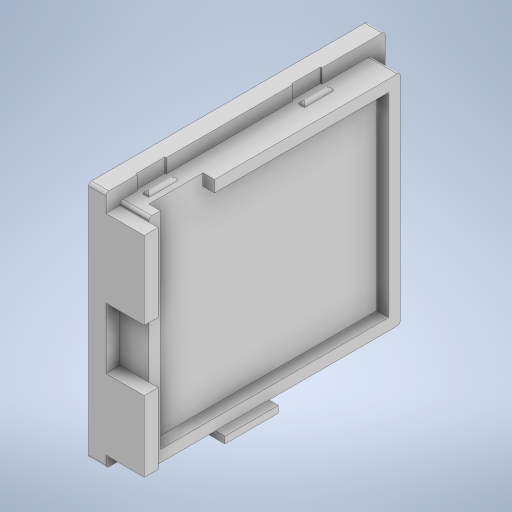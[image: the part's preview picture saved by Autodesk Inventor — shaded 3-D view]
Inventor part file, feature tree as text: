
AUTODESK INVENTOR PART (.ipt)
format: ipt  version: 2023 (Build 270158030, 158C)  size: 447,488 bytes
history: native  units: mm
features: extrude x13, sketch x13, fillet x6
ambient origin geometry x8: Origin, YZ Plane, XZ Plane, XY Plane, X Axis, Y Axis, Z Axis, Center Point
bodies: Solid1 (feature_tree)
feature tree (32):
  extrude  "Extrusion1"  Depth=48.11mm
  extrude  "Extrusion2"  Depth=43.31mm
  extrude  "PowerSocket"  Depth=2.4mm
  extrude  "RJ-12"  Depth=12.2mm
  extrude  "USB-C"  Depth=6.6mm TaperAngle=0.0deg
  extrude  "Extrusion7"  Depth=13.4mm
  extrude  "Extrusion8"  Depth=9.2mm
  fillet  "Fillet3"  Radius=13.9mm
  extrude  "Extrusion9"  Depth=2.0mm
  fillet  "Fillet4"  Radius=2.0mm
  extrude  "Extrusion10"  Depth=2.0mm
  fillet  "Fillet5"  Radius=30.0mm
  extrude  "Extrusion11"  Depth=2.0mm TaperAngle=0.0deg
  fillet  "Fillet6"  Radius=1.0mm
  fillet  "Fillet7"  Radius=5.0mm
  extrude  "TrimmWall"  Depth=0.5mm TaperAngle=0.0deg
  fillet  "Fillet8"  Radius=0.5mm
  extrude  "Oeffnungskerben1"  Depth=5.0mm
  extrude  "Oeffnungskerben2"  Depth=0.5mm TaperAngle=0.0deg
  sketch  "Sketch1"  dims[d0=42.0mm d1=48.11mm]
  sketch  "Sketch2"  dims[d2=3.0mm d3=0.0mm d4=43.31mm]
  sketch  "Sketch3"  dims[d6=2.4mm d7=2.4mm]
  sketch  "Sketch5"  dims[d8=3.0mm d9=0.0mm d12=12.2mm]
  sketch  "Sketch6"  dims[d13=2.8mm d14=6.6mm d15=0.0mm]
  sketch  "Sketch7"  dims[d20=2.0mm d21=13.4mm]
  sketch  "Sketch8"  dims[d23=6.6mm d24=0.0mm d25=9.2mm d26=13.9mm]
  sketch  "Sketch9"  dims[d27=6.6mm d28=0.0mm d29=2.0mm d30=2.0mm]
  sketch  "Sketch10"  dims[d31=2.0mm d32=2.0mm d33=30.0mm]
  sketch  "Sketch11"  dims[d34=2.0mm d35=2.0mm d36=0.0mm d37=1.0mm d38=5.0mm]
  sketch  "Sketch14"  dims[d39=5.5mm d41=0.5mm d42=0.0mm d43=0.5mm]
  sketch  "Sketch15"  dims[d44=1.0mm d45=5.0mm]
  sketch  "Sketch16"  dims[d47=11.0mm d48=0.5mm d49=0.0mm d50=0.5mm d51=1.0mm d52=5.0mm d54=11.0mm d55=0.5mm d56=0.0mm d57=0.5mm d58=1.0mm d59=1.0mm d60=1.0mm d61=1.0mm d62=5.0mm d63=1.0mm d64=5.5mm d65=0.5mm d66=0.0mm d67=0.5mm d68=0.5mm d75=3.1mm d76=0.83mm d77=0.0mm d78=0.5mm d79=5.0mm d80=5.0mm d81=0.25mm d82=0.0mm d83=5.0mm d84=5.0mm d85=0.25mm d86=0.0mm]
